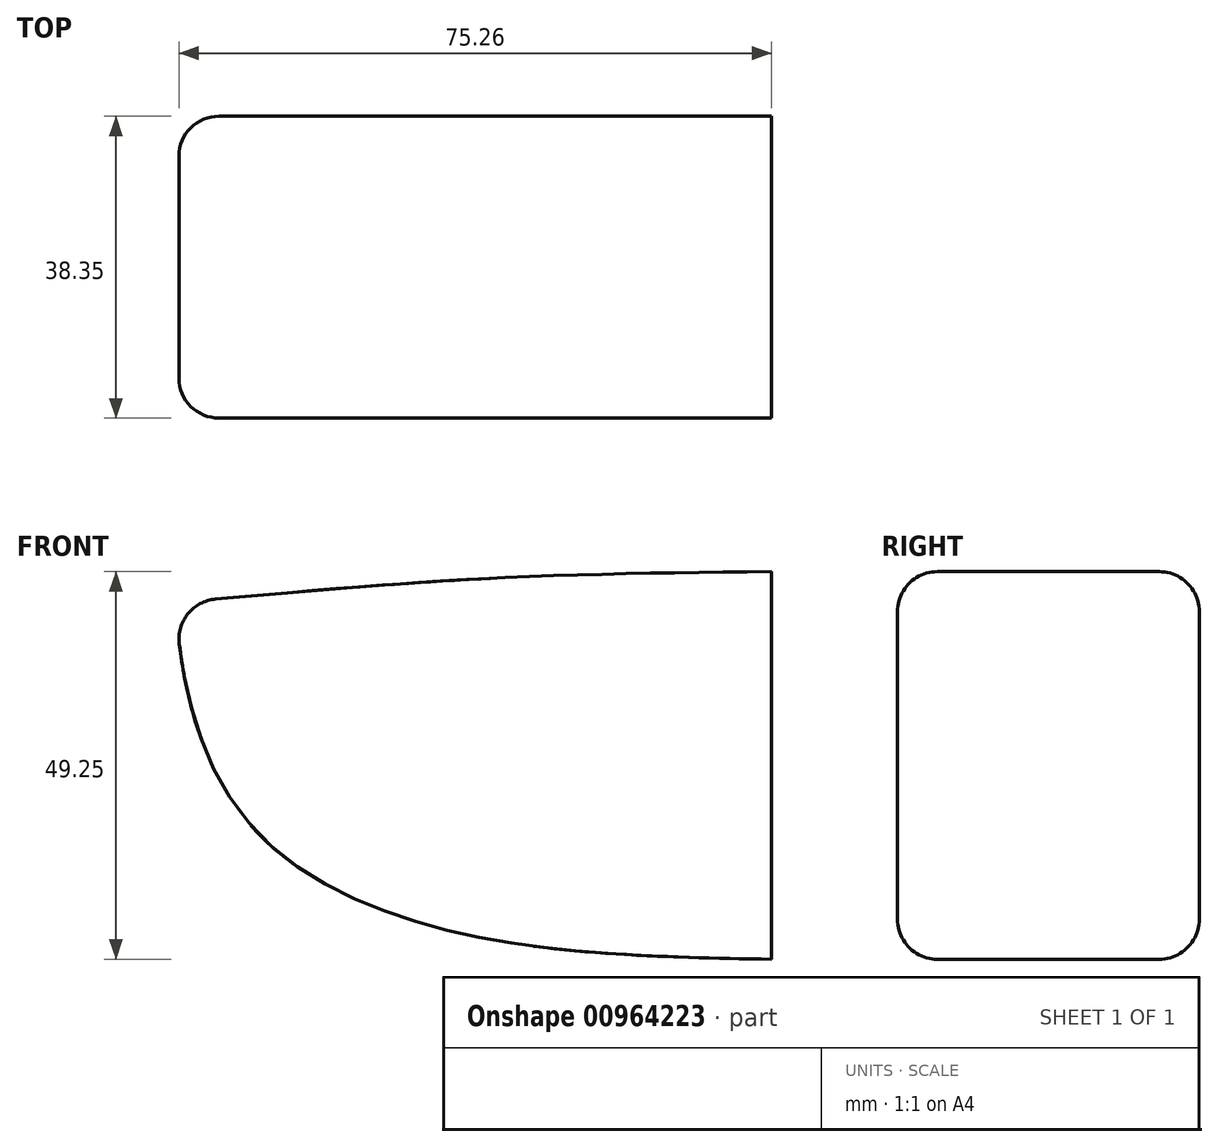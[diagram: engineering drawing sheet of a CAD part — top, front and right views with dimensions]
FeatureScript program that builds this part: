
annotation { "Feature Type Name" : "Feature", "Feature Type Description" : "" }
export const myFeature = defineFeature(function(context is Context, id is Id, definition is map)
    precondition{}
    {
        {
            var Q0;
            Q0=qCreatedBy(makeId("Front.planeOp"),FACE);
            var sketch = newSketch(context, id + "F0", { "sketchPlane" : qUnion([Q0])});
            skFitSpline(sketch, "E0.MirrorCS", {"points": [v(0, 0) * mm, v(-39.2, 3.22) * mm, v(-64.27, 15.07) * mm, v(-73.37, 30.87) * mm, v(-75.43, 42.03) * mm, v(-75.66, 45.3) * mm], "startDerivative": vector(-136.25, 2.71) * mm, "endDerivative": vector(-1.58, 32.47) * mm});
            skFitSpline(sketch, "E1", {"points": [v(-75.66, 45.3) * mm, v(-35.8, 48.39) * mm, v(0, 49.25) * mm], "startDerivative": vector(78.58, 7.11) * mm, "endDerivative": vector(72.68, 0.73) * mm});
            skLineSegment(sketch, "E2", {"start": v(0, 49.25) * mm, "end": v(0, 0) * mm});
            skPoint(sketch, "E3.MirrorCS.start.orphan", {"position": v(75.66, 45.3) * mm});
            skSolve(sketch);
        }
        {
            var Q0;
            Q0=makeQuery(id+"F0.imprint","IMPRINT",FACE,{"disambiguationData":[TD([[makeQuery(id+"F0.imprint","IMPRINT",EDGE,{"derivedFrom":sQuery(id+"F0.wireOp",EDGE,"E0.MirrorCS")}),-1.0]])]});
            extrude(context, id + "F1", {"entities" : qUnion([Q0]), "oppositeDirection" : true, "depth" : 38.35 * mm, "offsetDistance" : 25.4 * mm});
        }
        {
            var Q0;
            Q0=makeQuery(id+"F1.opExtrude","CAP_EDGE",EDGE,{"disambiguationData":[OSD([sQuery(id+"F0.wireOp",EDGE,"E1")])],"isStart":false});
            var Q1;
            Q1=makeQuery(id+"F1.opExtrude","SWEPT_EDGE",EDGE,{"disambiguationData":[OSD([sQuery(id+"F0.wireOp",EDGE,"E0.MirrorCS"),sQuery(id+"F0.wireOp",EDGE,"E1")])]});
            var Q2;
            Q2=makeQuery(id+"F1.opExtrude","CAP_EDGE",EDGE,{"disambiguationData":[OSD([sQuery(id+"F0.wireOp",EDGE,"E0.MirrorCS")])],"isStart":false});
            var Q3;
            Q3=makeQuery(id+"F1.opExtrude","CAP_EDGE",EDGE,{"disambiguationData":[OSD([sQuery(id+"F0.wireOp",EDGE,"E0.MirrorCS")])],"isStart":true});
            var Q4;
            Q4=makeQuery(id+"F1.opExtrude","CAP_EDGE",EDGE,{"disambiguationData":[OSD([sQuery(id+"F0.wireOp",EDGE,"E1")])],"isStart":true});
            fillet(context, id + "F2", {"entities" : qUnion([Q0, Q1, Q2, Q3, Q4]), "radius" : 5.08 * mm, "tangentPropagation" : true, "allowEdgeOverflow" : false});
        }
    });
